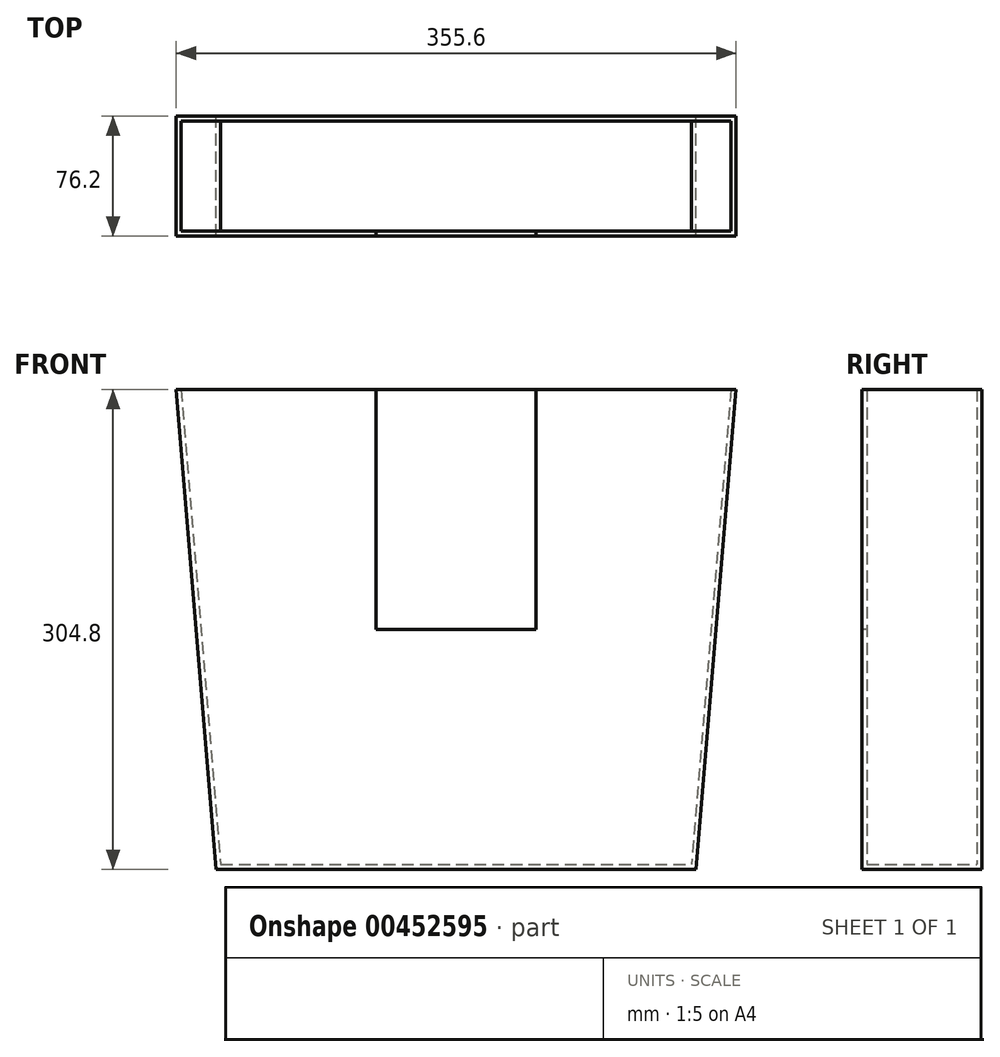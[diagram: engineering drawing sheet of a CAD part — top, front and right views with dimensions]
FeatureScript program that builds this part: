
annotation { "Feature Type Name" : "Feature", "Feature Type Description" : "" }
export const myFeature = defineFeature(function(context is Context, id is Id, definition is map)
    precondition{}
    {
        {
            var Q0;
            Q0=qCreatedBy(makeId("Front.planeOp"),FACE);
            var sketch = newSketch(context, id + "F0", { "sketchPlane" : qUnion([Q0])});
            skLineSegment(sketch, "E0", {"start": v(0, 0) * mm, "end": v(-177.8, 0) * mm});
            skLineSegment(sketch, "E1", {"start": v(-177.8, 0) * mm, "end": v(-152.4, -304.8) * mm});
            skLineSegment(sketch, "E2", {"start": v(-152.4, -304.8) * mm, "end": v(0, -304.8) * mm});
            skLineSegment(sketch, "E3", {"start": v(0, 0) * mm, "end": v(177.8, 0) * mm});
            skLineSegment(sketch, "E4", {"start": v(177.8, 0) * mm, "end": v(152.4, -304.8) * mm});
            skLineSegment(sketch, "E5", {"start": v(152.4, -304.8) * mm, "end": v(0, -304.8) * mm});
            skSolve(sketch);
        }
        {
            var Q0;
            Q0=makeQuery(id+"F0.imprint","IMPRINT",FACE,{"disambiguationData":[TD([[makeQuery(id+"F0.imprint","IMPRINT",EDGE,{"derivedFrom":sQuery(id+"F0.wireOp",EDGE,"E0")}),1.0]])]});
            extrude(context, id + "F1", {"entities" : qUnion([Q0]), "depth" : 76.2 * mm});
        }
        {
            var Q0;
            Q0=makeQuery(id+"F1.opExtrude","SWEPT_FACE",FACE,{"disambiguationData":[OSD([sQuery(id+"F0.wireOp",EDGE,"E0"),sQuery(id+"F0.wireOp",EDGE,"E3")])]});
            shell(context, id + "F2", {"entities" : qUnion([Q0]), "thickness" : 3.17 * mm});
        }
        {
            var Q0;
            Q0=makeQuery(id+"F1.opExtrude","CAP_FACE",FACE,{"disambiguationData":[OSD([sQuery(id+"F0.wireOp",EDGE,"E0"),sQuery(id+"F0.wireOp",EDGE,"E1"),sQuery(id+"F0.wireOp",EDGE,"E2"),sQuery(id+"F0.wireOp",EDGE,"E3"),sQuery(id+"F0.wireOp",EDGE,"E4"),sQuery(id+"F0.wireOp",EDGE,"E5")])],"isStart":false});
            var sketch = newSketch(context, id + "F3", { "sketchPlane" : qUnion([Q0])});
            skLineSegment(sketch, "E6.bottom", {"start": v(-50.8, 0) * mm, "end": v(50.8, 0) * mm});
            skLineSegment(sketch, "E6.top", {"start": v(-50.8, -152.4) * mm, "end": v(50.8, -152.4) * mm});
            skLineSegment(sketch, "E6.left", {"start": v(-50.8, 0) * mm, "end": v(-50.8, -152.4) * mm});
            skLineSegment(sketch, "E6.right", {"start": v(50.8, 0) * mm, "end": v(50.8, -152.4) * mm});
            skLineSegment(sketch, "E7", {"start": v(-50.8, -76.2) * mm, "end": v(50.8, -76.2) * mm});
            skLineSegment(sketch, "E8", {"start": v(0, -152.4) * mm, "end": v(0, 0) * mm});
            skSolve(sketch);
        }
        {
            var Q0;
            {var subQ0=sQuery(id+"F3.wireOp",EDGE,"E6.left");var subQ1=sQuery(id+"F3.wireOp",EDGE,"E6.top");var subQ2=makeQuery(id+"F3.imprint","INTERSECT",VERTEX,{"derivedFrom":[subQ1,subQ0]});Q0=makeQuery(id+"F3.imprint","IMPRINT",FACE,{"disambiguationData":[TD([[makeQuery(id+"F3.imprint","IMPRINT",EDGE,{"disambiguationData":[TD([[subQ2,-1.0]])],"derivedFrom":subQ1}),1.0]])]});}
            var Q1;
            {var subQ0=sQuery(id+"F3.wireOp",EDGE,"E6.left");var subQ5=sQuery(id+"F3.wireOp",EDGE,"E7");var subQ6=makeQuery(id+"F3.imprint","INTERSECT",VERTEX,{"derivedFrom":[subQ0,subQ5]});Q1=makeQuery(id+"F3.imprint","IMPRINT",FACE,{"disambiguationData":[TD([[makeQuery(id+"F3.imprint","IMPRINT",EDGE,{"disambiguationData":[TD([[subQ6,-1.0]])],"derivedFrom":subQ5}),1.0]])]});}
            var Q2;
            {var subQ0=sQuery(id+"F3.wireOp",EDGE,"E6.right");var subQ5=sQuery(id+"F3.wireOp",EDGE,"E7");var subQ6=makeQuery(id+"F3.imprint","INTERSECT",VERTEX,{"derivedFrom":[subQ0,subQ5]});Q2=makeQuery(id+"F3.imprint","IMPRINT",FACE,{"disambiguationData":[TD([[makeQuery(id+"F3.imprint","IMPRINT",EDGE,{"disambiguationData":[TD([[subQ6,1.0]])],"derivedFrom":subQ5}),1.0]])]});}
            var Q3;
            {var subQ0=sQuery(id+"F3.wireOp",EDGE,"E6.right");var subQ1=sQuery(id+"F3.wireOp",EDGE,"E6.top");var subQ2=makeQuery(id+"F3.imprint","INTERSECT",VERTEX,{"derivedFrom":[subQ1,subQ0]});Q3=makeQuery(id+"F3.imprint","IMPRINT",FACE,{"disambiguationData":[TD([[makeQuery(id+"F3.imprint","IMPRINT",EDGE,{"disambiguationData":[TD([[subQ2,1.0]])],"derivedFrom":subQ1}),1.0]])]});}
            var Q4;
            Q4=sQuery(id+"F3.wireOp",EDGE,"E8");
            extrude(context, id + "F4", {"entities" : qUnion([Q0, Q1, Q2, Q3]), "operationType" : NewBodyOperationType.REMOVE, "surfaceEntities" : qUnion([Q4]), "oppositeDirection" : true, "depth" : 25.4 * mm});
        }
    });
